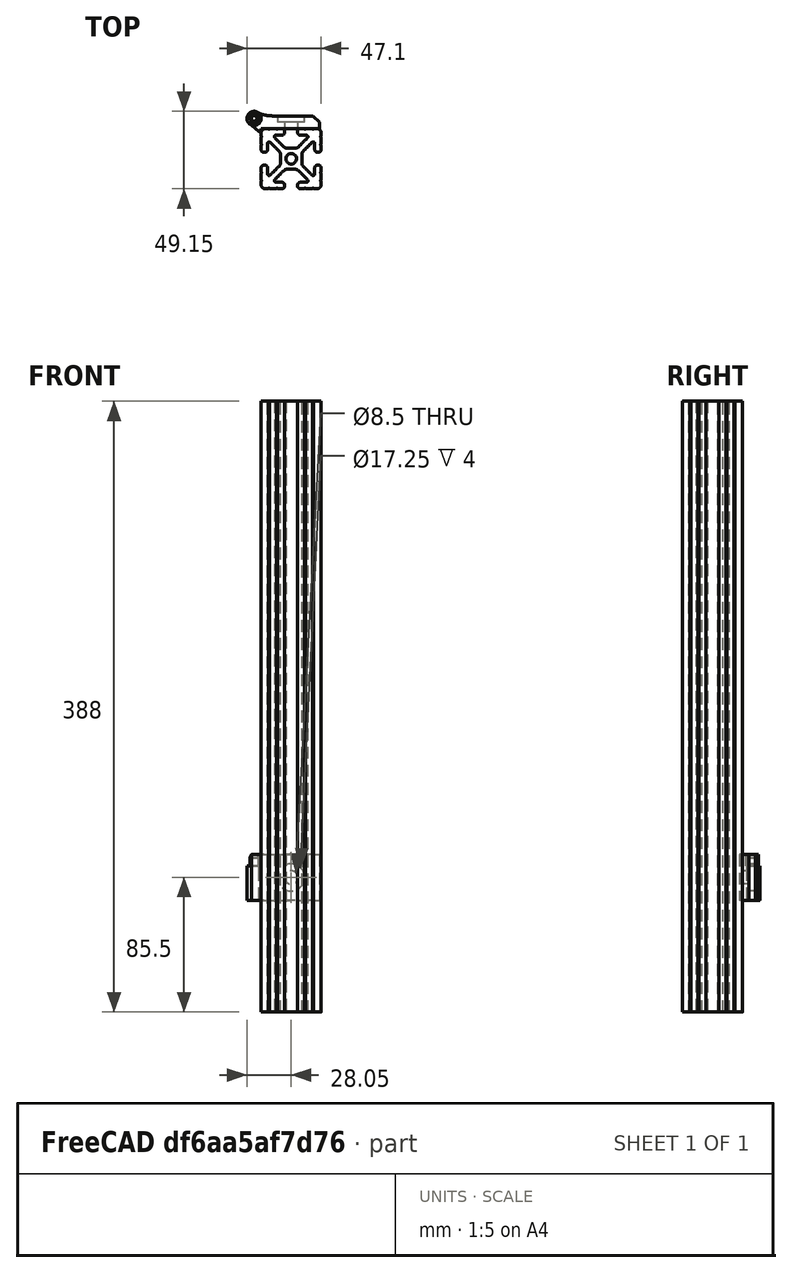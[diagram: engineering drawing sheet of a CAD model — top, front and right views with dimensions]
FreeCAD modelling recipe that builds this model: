
FCSTD DOCUMENT  (FreeCAD 0.18R)
Label: rambo-lower-hinge
License: All rights reserved
LicenseURL: http://en.wikipedia.org/wiki/All_rights_reserved
objects: Sketcher::SketchObject×6, PartDesign::Pad×3, PartDesign::Pocket×2, PartDesign::Revolution×1, PartDesign::Body×1, Part::Feature×1, Mesh::Feature×1
note: 20 computed .brp shape members not serialized (recipe doc carries the construction recipe); baked Part::Feature solids carry a one-line shape summary decoded from their .brp

FEATURE [Sketcher::SketchObject] Sketch
  MapMode = 5
  Support = -> [XY_Plane]
  sketch-geometry (9):
    g0: LineSegment StartX=0 StartY=2 StartZ=0 EndX=37 EndY=2 EndZ=0
    g1: LineSegment StartX=37 StartY=2 StartZ=0 EndX=37 EndY=6 EndZ=0
    g2: LineSegment StartX=33 StartY=10 StartZ=0 EndX=37 EndY=6 EndZ=0
    g3: LineSegment StartX=-6.1 StartY=4.29405 StartZ=0 EndX=-1.35 EndY=0.0759839 EndZ=0
    g4: LineSegment StartX=-1.15 StartY=0 StartZ=0 EndX=0 EndY=0 EndZ=0
    g5: ArcOfCircle CenterX=-4.5 CenterY=8.5 CenterZ=0 NormalX=0 NormalY=0 NormalZ=1 AngleXU=0 Radius=4.5 StartAngle=4.34888 EndAngle=6.62302
    g6: ArcOfCircle CenterX=-1.15 CenterY=0.301206 CenterZ=0 NormalX=0 NormalY=0 NormalZ=1 AngleXU=0 Radius=0.301206 StartAngle=3.98624 EndAngle=4.71239
    g7: LineSegment StartX=0 StartY=2 StartZ=0 EndX=0 EndY=0 EndZ=0
    g8: LineSegment StartX=33 StartY=10 StartZ=0 EndX=-0.257359 EndY=10 EndZ=0
  constraints (26):
    c: Horizontal(g0)
    c: DistanceX(g0,g0) = 37
    c: Coincident(g1,g0)
    c: Vertical(g1)
    c: DistanceY(g0,g1) = 4
    c: PointOnObject(g0,g-2)
    c: DistanceY(g-1,g0) = 2
    c: Coincident(g2,g1)
    c: Coincident(g4,g-1)
    c: DistanceY(g4,g5) = 8.5
    c: DistanceX(g5,g4) = 4.5
    c: Coincident(g5,g3)
    c: DistanceX(g3,g4) = 6.1
    c: Radius(g5) = 4.5
    c: Tangent(g3,g6) = -1.5708
    c: Tangent(g4,g6) = -1.5708
    c: DistanceX(g3,g4) = 0.2
    c: PointOnObject(g4,g-1)
    c: DistanceX(g4,g4) = 1.15
    c: Coincident(g7,g0)
    c: Coincident(g7,g4)
    c: DistanceY(g0,g2) = 8
    c: Coincident(g8,g5)
    c: Horizontal(g8)
    c: Coincident(g8,g2)
    c: DistanceX(g2,g1) = 4
FEATURE [PartDesign::Pad] Pad
  Length = 29
  Length2 = 100
  Profile = -> Sketch
  Reversed = true
  Type = 0
FEATURE [Sketcher::SketchObject] Sketch001
  AttachmentOffset = pos=(-4.5,-9.3,-8.5) rot=(0,0,1;0rad)
  MapMode = 5
  Placement = pos=(-4.5,8.5,-9.3) rot=(1,0,0;1.5708rad)
  Support = -> [XZ_Plane]
  sketch-geometry (8):
    g0: LineSegment StartX=-1.75 StartY=9.3 StartZ=0 EndX=0 EndY=9.3 EndZ=0
    g1: LineSegment StartX=-1.75 StartY=9.3 StartZ=0 EndX=-2.5 EndY=7.15 EndZ=0
    g2: LineSegment StartX=-2.5 StartY=7.15 StartZ=0 EndX=-2.5 EndY=2 EndZ=0
    g3: LineSegment StartX=0 StartY=0 StartZ=0 EndX=0 EndY=9.3 EndZ=0
    g4: LineSegment StartX=-2.5 StartY=2 StartZ=0 EndX=-4.5 EndY=2 EndZ=0
    g5: LineSegment StartX=-4.5 StartY=2 StartZ=0 EndX=-4.5 EndY=0 EndZ=0
    g6: LineSegment StartX=-4.5 StartY=0 StartZ=0 EndX=0 EndY=0 EndZ=0
    g7: LineSegment StartX=0 StartY=9.3 StartZ=0 EndX=0 EndY=0 EndZ=0
  constraints (23):
    c: Horizontal(g0)
    c: Coincident(g2,g1)
    c: Vertical(g2)
    c: Coincident(g3,g0)
    c: Vertical(g3)
    c: Coincident(g0,g1)
    c: DistanceX(g0,g0) = 1.75
    c: PointOnObject(g3,g-2)
    c: DistanceX(g1,g3) = 2.5
    c: DistanceY(g1,g0) = 2.15
    c: DistanceY(g2,g1) = 5.15
    c: Coincident(g4,g2)
    c: Horizontal(g4)
    c: DistanceX(g4,g2) = 2
    c: Coincident(g5,g4)
    c: PointOnObject(g5,g-1)
    c: Vertical(g5)
    c: Coincident(g6,g5)
    c: Horizontal(g6)
    c: DistanceY(g5,g4) = 2
    c: Coincident(g7,g0)
    c: Coincident(g7,g6)
    c: Coincident(g3,g6)
FEATURE [PartDesign::Revolution] Revolution
  Angle = 360
  Axis = (0,-2e-16,1)
  Base = (-4.5,8.5,-9.3)
  BaseFeature = -> Pad
  Profile = -> Sketch001
  ReferenceAxis = -> Sketch001 [V_Axis]
FEATURE [Sketcher::SketchObject] Sketch003
  AttachmentOffset = pos=(0,0,-29) rot=(0,0,1;0rad)
  MapMode = 5
  Placement = pos=(0,0,-29) rot=(0,0,1;0rad)
  Support = -> [XY_Plane]
  sketch-geometry (1):
    g0: Circle CenterX=-4.5 CenterY=8.5 CenterZ=0 NormalX=0 NormalY=0 NormalZ=1 AngleXU=0 Radius=4.5
  constraints (3):
    c: Diameter(g0) = 9
    c: DistanceX(g0,g-1) = 4.5
    c: DistanceY(g-1,g0) = 8.5
FEATURE [PartDesign::Pad] Pad001
  BaseFeature = -> Revolution
  Length = 19.7
  Length2 = 100
  Profile = -> Sketch003
  Type = 0
FEATURE [Sketcher::SketchObject] Sketch004
  MapMode = 5
  Support = -> [XY_Plane]
  sketch-geometry (9):
    g0: ArcOfCircle CenterX=-4.5 CenterY=8.5 CenterZ=0 NormalX=0 NormalY=0 NormalZ=1 AngleXU=0 Radius=4.5 StartAngle=0.339837 EndAngle=0.891123
    g1: Circle [constr] CenterX=-1.67157 CenterY=12 CenterZ=0 NormalX=0 NormalY=0 NormalZ=1 AngleXU=0 Radius=0.8
    g2: Circle [constr] CenterX=1.778 CenterY=10 CenterZ=0 NormalX=0 NormalY=0 NormalZ=1 AngleXU=0 Radius=0.8
    g3: Circle [constr] CenterX=9.875 CenterY=10 CenterZ=0 NormalX=0 NormalY=0 NormalZ=1 AngleXU=0 Radius=0.8
    g4: BSplineCurve PolesCount=3 KnotsCount=2 Degree=2 IsPeriodic=0
    g5: GeomPoint [constr] X=-1.67157 Y=12 Z=0
    g6: GeomPoint [constr] X=9.875 Y=10 Z=0
    g7: LineSegment StartX=-0.257359 StartY=10 StartZ=0 EndX=1.778 EndY=10 EndZ=0
    g8: LineSegment StartX=1.778 StartY=10 StartZ=0 EndX=9.875 EndY=10 EndZ=0
  constraints (21):
    c: Diameter(g0) = 9
    c: DistanceX(g0,g-1) = 4.5
    c: DistanceY(g-1,g0) = 8.5
    c: Radius(g1) = 0.8
    c: Equal(g1,g2)
    c: Equal(g1,g3)
    c: InternalAlignment(g1,g4)
    c: InternalAlignment(g2,g4)
    c: InternalAlignment(g3,g4)
    c: InternalAlignment(g5,g4)
    c: InternalAlignment(g6,g4)
    c: DistanceX(g-1,g4) = 9.875
    c: DistanceY(g4,g2) = 0
    c: Horizontal(g7)
    c: Coincident(g7,g2)
    c: Coincident(g0,g7)
    c: Coincident(g0,g4)
    c: DistanceY(g-1,g4) = 10
    c: DistanceY(g0,g0) = 2
    c: Coincident(g8,g4)
    c: Horizontal(g8)
FEATURE [PartDesign::Pad] Pad002
  BaseFeature = -> Pad001
  Length = 29
  Length2 = 100
  Profile = -> Sketch004
  Reversed = true
  Type = 0
FEATURE [Sketcher::SketchObject] Sketch005
  MapMode = 5
  Placement = pos=(0,0,0) rot=(1,0,0;1.5708rad)
  Support = -> [XZ_Plane]
  sketch-geometry (1):
    g0: Circle CenterX=19.05 CenterY=-14.5 CenterZ=0 NormalX=0 NormalY=0 NormalZ=1 AngleXU=0 Radius=4.25
  constraints (3):
    c: Diameter(g0) = 8.5
    c: DistanceX(g-1,g0) = 19.05
    c: DistanceY(g0,g-1) = 14.5
FEATURE [PartDesign::Pocket] Pocket
  BaseFeature = -> Pad002
  Length = 5
  Length2 = 100
  Profile = -> Sketch005
  Type = 1
FEATURE [Sketcher::SketchObject] Sketch006
  AttachmentOffset = pos=(0,0,-6) rot=(0,0,1;0rad)
  MapMode = 5
  Placement = pos=(0,6,1.3e-15) rot=(1,0,0;1.5708rad)
  Support = -> [XZ_Plane]
  sketch-geometry (1):
    g0: Circle CenterX=19.05 CenterY=-14.5 CenterZ=0 NormalX=0 NormalY=0 NormalZ=1 AngleXU=0 Radius=8.625
  constraints (3):
    c: Diameter(g0) = 17.25
    c: DistanceX(g-1,g0) = 19.05
    c: DistanceY(g0,g-1) = 14.5
FEATURE [PartDesign::Pocket] Pocket001
  BaseFeature = -> Pocket
  Length = 5
  Length2 = 100
  Profile = -> Sketch006
  Type = 0
FEATURE [PartDesign::Body] Body  label="rambo-lower-hinge"
  Group = -> [Sketch,Pad,Sketch001,Revolution,Sketch003,Pad001,Sketch004,Pad002,Sketch005,Pocket,Sketch006,Pocket001]
  Origin = -> Origin
  Tip = -> Pocket001
FEATURE [Part::Feature] _515_extrusion_388_000mm
  Placement = pos=(-127,-74.25,-100) rot=(0,0,1;0rad)
  shape: bbox 38.1 x 38.1 x 388 mm, 113 faces (baked)
FEATURE [Mesh::Feature] Einsy_doors  label="Einsy-doors"
  Placement = pos=(-75.75,14.5,-51) rot=(0,0,1;4.71239rad)
